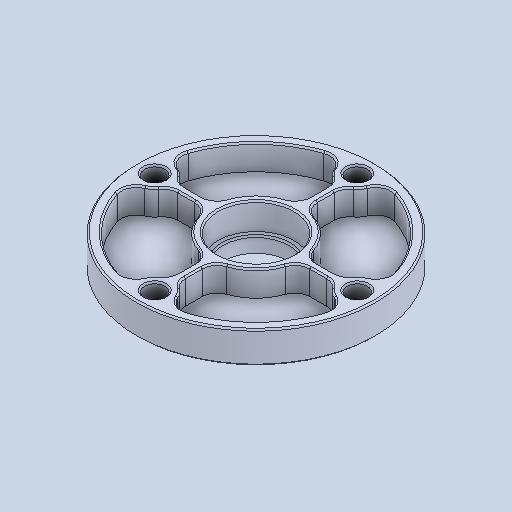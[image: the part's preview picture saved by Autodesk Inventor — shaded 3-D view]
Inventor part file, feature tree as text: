
AUTODESK INVENTOR PART (.ipt)
format: ipt  version: 2023.2 (Build 272271000, 271)  size: 276,992 bytes
history: native  units: in
note: dims shown in document units (in); Inventor stores cm internally (conversion verified against a paired STEP export)
features: chamfer x1
ambient origin geometry x8: Origin, YZ Plane, XZ Plane, XY Plane, X Axis, Y Axis, Z Axis, Center Point
bodies: Solid1 (feature_tree)
feature tree (1):
  chamfer  "Chamfer1"  [1 undecoded]
note: 1 required parameter value undecoded (feature->parameter linkage not recoverable at this tier; creation-order binding heuristic only, values carry confidence <= 0.55)
